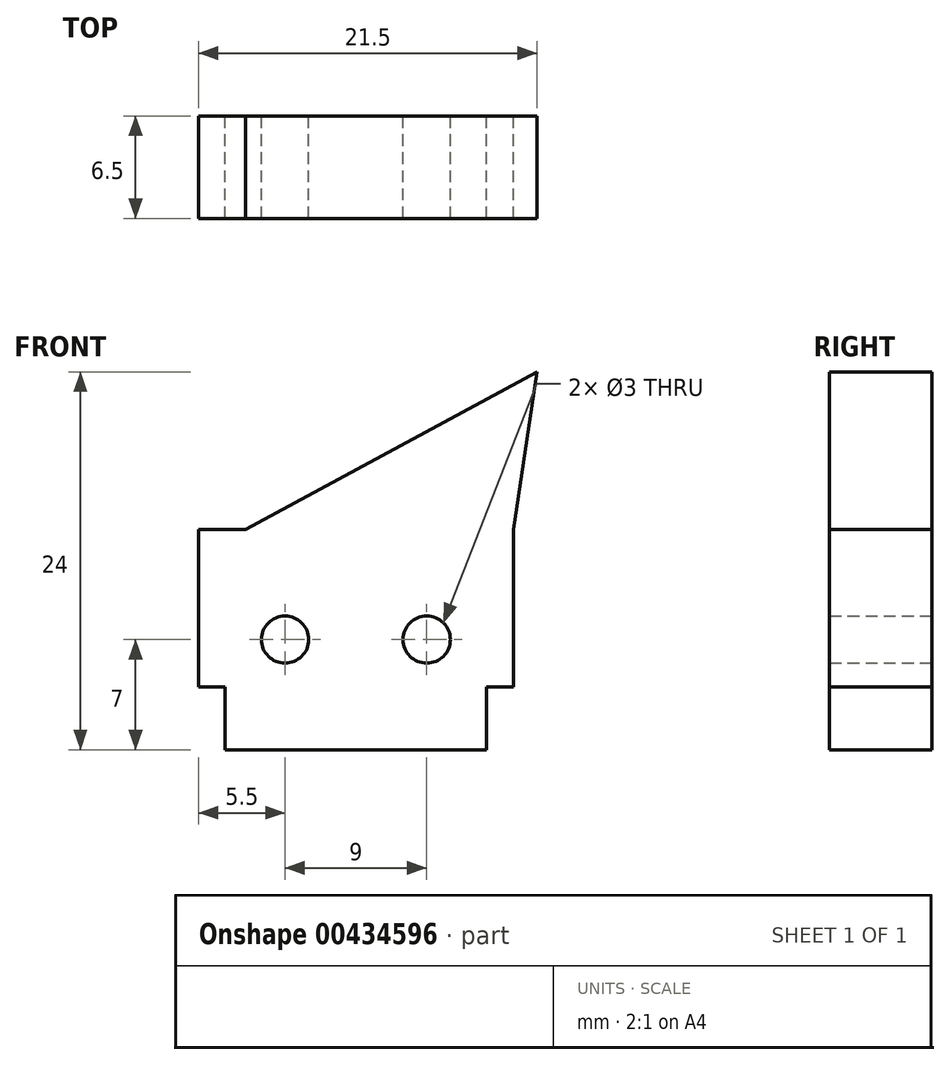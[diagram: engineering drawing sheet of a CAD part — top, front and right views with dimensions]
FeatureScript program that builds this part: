
annotation { "Feature Type Name" : "Feature", "Feature Type Description" : "" }
export const myFeature = defineFeature(function(context is Context, id is Id, definition is map)
    precondition{}
    {
        {
            var Q0;
            Q0=qCreatedBy(makeId("Front.planeOp"),FACE);
            var sketch = newSketch(context, id + "F0", { "sketchPlane" : qUnion([Q0])});
            skLineSegment(sketch, "E0.bottom", {"start": v(0, 0) * mm, "end": v(20, 0) * mm});
            skLineSegment(sketch, "E0.top", {"start": v(0, 10) * mm, "end": v(20, 10) * mm});
            skLineSegment(sketch, "E0.left", {"start": v(0, 0) * mm, "end": v(0, 10) * mm});
            skLineSegment(sketch, "E0.right", {"start": v(20, 0) * mm, "end": v(20, 10) * mm});
            skLineSegment(sketch, "E1.bottom", {"start": v(1.7, 0) * mm, "end": v(18.3, 0) * mm});
            skLineSegment(sketch, "E1.top", {"start": v(1.7, -4) * mm, "end": v(18.3, -4) * mm});
            skLineSegment(sketch, "E1.left", {"start": v(1.7, 0) * mm, "end": v(1.7, -4) * mm});
            skLineSegment(sketch, "E1.right", {"start": v(18.3, 0) * mm, "end": v(18.3, -4) * mm});
            skLineSegment(sketch, "E2", {"start": v(3, 10) * mm, "end": v(21.5, 20) * mm});
            skLineSegment(sketch, "E3", {"start": v(21.5, 20) * mm, "end": v(20, 10) * mm});
            skCircle(sketch, "E4", {"center": v(5.5, 3) * mm, "radius": 1.5 * mm});
            skCircle(sketch, "E5", {"center": v(14.5, 3) * mm, "radius": 1.5 * mm});
            skSolve(sketch);
        }
        {
            var Q0;
            Q0 = qSketchRegion(id + "F0", true);
            extrude(context, id + "F1", {"entities" : qUnion([Q0]), "depth" : 6.5 * mm});
        }
    });
